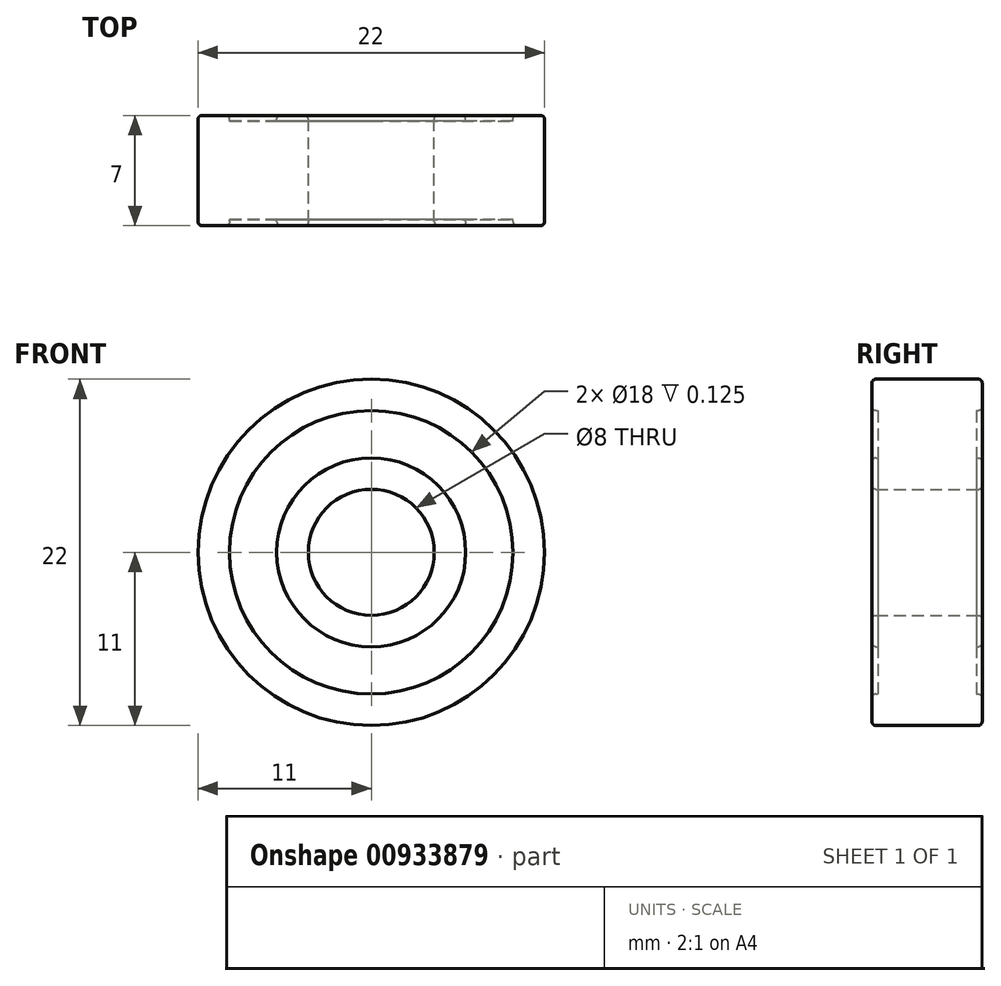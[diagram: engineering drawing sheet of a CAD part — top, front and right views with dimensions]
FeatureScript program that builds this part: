
annotation { "Feature Type Name" : "Feature", "Feature Type Description" : "" }
export const myFeature = defineFeature(function(context is Context, id is Id, definition is map)
    precondition{}
    {
        {
            var Q0;
            Q0=qCreatedBy(makeId("Top.planeOp"),FACE);
            var sketch = newSketch(context, id + "F0", { "sketchPlane" : qUnion([Q0])});
            skLineSegment(sketch, "E0", {"start": v(0, 63.35) * mm, "end": v(0, -63.35) * mm, "construction": true});
            skSolve(sketch);
        }
        {
            assignVariable(context, id + "F1", {"name" : "RadiusEdge", "anyValue" : .25});
        }
        {
            var Q0;
            Q0=qCreatedBy(makeId("Right.planeOp"),FACE);
            var sketch = newSketch(context, id + "F2", { "sketchPlane" : qUnion([Q0])});
            skLineSegment(sketch, "E1.bottom", {"start": v(3.5, 9) * mm, "end": v(3.12, 9) * mm});
            skLineSegment(sketch, "E1.top", {"start": v(3.5, 11) * mm, "end": v(-3.5, 11) * mm});
            skLineSegment(sketch, "E1.left", {"start": v(3.5, 9) * mm, "end": v(3.5, 11) * mm});
            skLineSegment(sketch, "E1.right", {"start": v(-3.5, 9) * mm, "end": v(-3.5, 11) * mm});
            skPoint(sketch, "E1.middle", {"position": v(0, 10) * mm});
            skLineSegment(sketch, "E2.left", {"start": v(3.12, 9) * mm, "end": v(3.13, 6) * mm});
            skLineSegment(sketch, "E2.right", {"start": v(-3.13, 9) * mm, "end": v(-3.12, 6) * mm});
            skPoint(sketch, "E2.middle", {"position": v(0, 7.5) * mm});
            skLineSegment(sketch, "E3.trimOffspring", {"start": v(-3.13, 9) * mm, "end": v(-3.5, 9) * mm});
            skLineSegment(sketch, "E4.bottom", {"start": v(3.5, 6) * mm, "end": v(3.13, 6) * mm});
            skLineSegment(sketch, "E4.top", {"start": v(3.5, 4) * mm, "end": v(-3.5, 4) * mm});
            skLineSegment(sketch, "E4.left", {"start": v(3.5, 6) * mm, "end": v(3.5, 4) * mm});
            skLineSegment(sketch, "E4.right", {"start": v(-3.5, 6) * mm, "end": v(-3.5, 4) * mm});
            skPoint(sketch, "E4.middle", {"position": v(0, 5) * mm});
            skLineSegment(sketch, "E5.trimOffspring", {"start": v(-3.12, 6) * mm, "end": v(-3.5, 6) * mm});
            skSolve(sketch);
        }
        {
            var Q0;
            Q0 = qSketchRegion(id + "F2", true);
            var Q1;
            Q1=sQuery(id+"F0.wireOp",EDGE,"E0");
            revolve(context, id + "F3", {"surfaceOperationType" : NewSurfaceOperationType.NEW, "entities" : qUnion([Q0]), "axis" : qUnion([Q1]), "revolveType" : RevolveType.FULL});
        }
        {
            var Q0;
            Q0=makeQuery(id+"F3.opRevolve","SWEPT_EDGE",EDGE,{"disambiguationData":[OSD([sQuery(id+"F2.wireOp",EDGE,"E1.top"),sQuery(id+"F2.wireOp",EDGE,"E1.right")])]});
            var Q1;
            Q1=makeQuery(id+"F3.opRevolve","SWEPT_EDGE",EDGE,{"disambiguationData":[OSD([sQuery(id+"F2.wireOp",EDGE,"E1.right"),sQuery(id+"F2.wireOp",EDGE,"E3.trimOffspring")])]});
            var Q2;
            Q2=makeQuery(id+"F3.opRevolve","SWEPT_EDGE",EDGE,{"disambiguationData":[OSD([sQuery(id+"F2.wireOp",EDGE,"E4.right"),sQuery(id+"F2.wireOp",EDGE,"E5.trimOffspring")])]});
            var Q3;
            Q3=makeQuery(id+"F3.opRevolve","SWEPT_EDGE",EDGE,{"disambiguationData":[OSD([sQuery(id+"F2.wireOp",EDGE,"E4.top"),sQuery(id+"F2.wireOp",EDGE,"E4.right")])]});
            var Q4;
            Q4=makeQuery(id+"F3.opRevolve","SWEPT_EDGE",EDGE,{"disambiguationData":[OSD([sQuery(id+"F2.wireOp",EDGE,"E4.top"),sQuery(id+"F2.wireOp",EDGE,"E4.left")])]});
            var Q5;
            Q5=makeQuery(id+"F3.opRevolve","SWEPT_EDGE",EDGE,{"disambiguationData":[OSD([sQuery(id+"F2.wireOp",EDGE,"E4.bottom"),sQuery(id+"F2.wireOp",EDGE,"E4.left")])]});
            var Q6;
            Q6=makeQuery(id+"F3.opRevolve","SWEPT_EDGE",EDGE,{"disambiguationData":[OSD([sQuery(id+"F2.wireOp",EDGE,"E1.bottom"),sQuery(id+"F2.wireOp",EDGE,"E1.left")])]});
            var Q7;
            Q7=makeQuery(id+"F3.opRevolve","SWEPT_EDGE",EDGE,{"disambiguationData":[OSD([sQuery(id+"F2.wireOp",EDGE,"E1.top"),sQuery(id+"F2.wireOp",EDGE,"E1.left")])]});
            fillet(context, id + "F4", {"entities" : qUnion([Q0, Q1, Q2, Q3, Q4, Q5, Q6, Q7]), "radius" : (getVariable(context, 'RadiusEdge')) * mm, "tangentPropagation" : true, "allowEdgeOverflow" : false});
        }
    });
